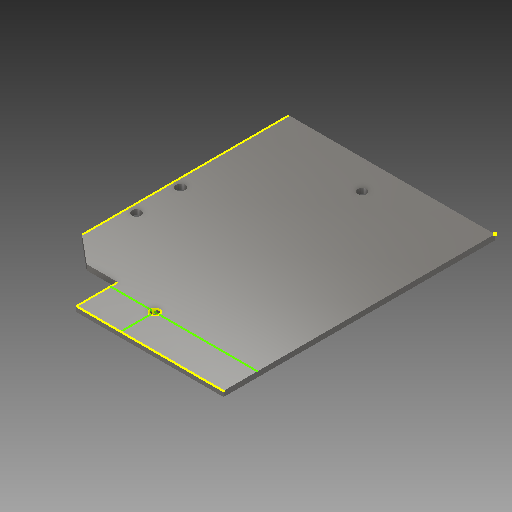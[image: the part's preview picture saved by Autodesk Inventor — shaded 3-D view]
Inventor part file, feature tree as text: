
AUTODESK INVENTOR PART (.ipt)
format: ipt  version: 2017 (Build 210142000, 142)  size: 119,296 bytes
history: native  units: in
note: dims shown in document units (in); Inventor stores cm internally (conversion verified against a paired STEP export)
features: sketch x5, other x3
ambient origin geometry x8: Origin, YZ Plane, XZ Plane, XY Plane, X Axis, Y Axis, Z Axis, Center Point
bodies: Solid1 (feature_tree)
feature tree (8):
  other  "flywheel plate.ipt"
  sketch  "Sketch4"
  sketch  "Sketch5"
  other  "Solid1::flywheel plate.ipt"
  other  "TaggingFeature1"
  sketch  "Sketch1"  dims[d0=0.3937in]
  sketch  "Sketch2"
  sketch  "Sketch3"
